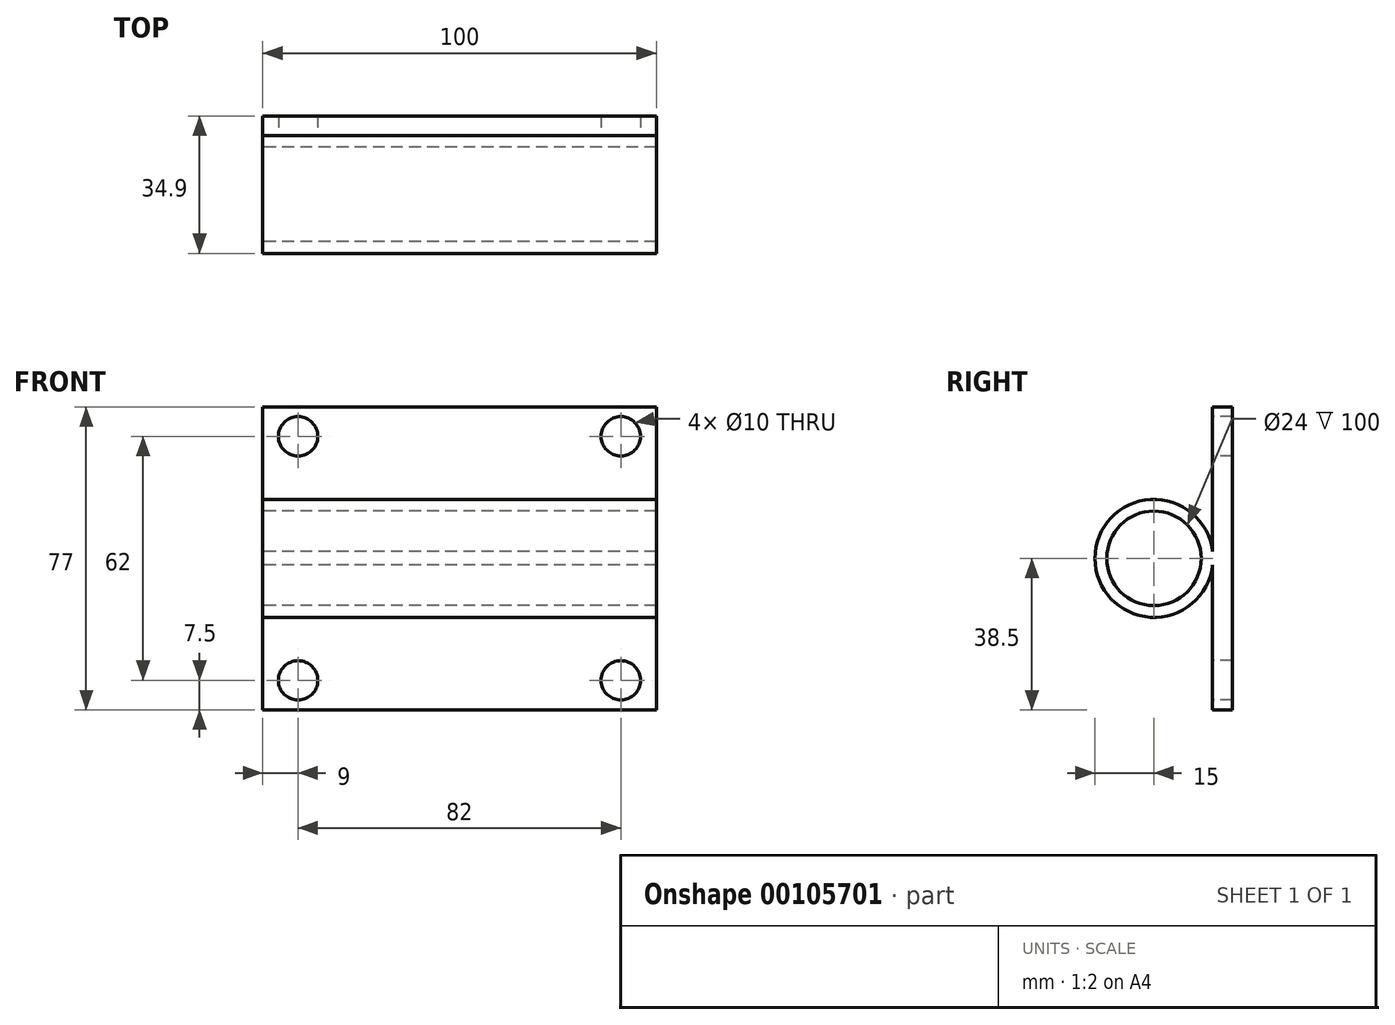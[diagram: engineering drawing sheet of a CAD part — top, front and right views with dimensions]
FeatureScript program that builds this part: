
annotation { "Feature Type Name" : "Feature", "Feature Type Description" : "" }
export const myFeature = defineFeature(function(context is Context, id is Id, definition is map)
    precondition{}
    {
        {
            var Q0;
            Q0=qCreatedBy(makeId("Front.planeOp"),FACE);
            var sketch = newSketch(context, id + "F0", { "sketchPlane" : qUnion([Q0])});
            skLineSegment(sketch, "E0.bottom", {"start": v(0, 0) * mm, "end": v(-100, 0) * mm});
            skLineSegment(sketch, "E0.top", {"start": v(0, 77) * mm, "end": v(-100, 77) * mm});
            skLineSegment(sketch, "E0.left", {"start": v(0, 0) * mm, "end": v(0, 77) * mm});
            skLineSegment(sketch, "E0.right", {"start": v(-100, 0) * mm, "end": v(-100, 77) * mm});
            skSolve(sketch);
        }
        {
            var Q0;
            Q0=makeQuery(id+"F0.imprint","IMPRINT",FACE,{"disambiguationData":[TD([[makeQuery(id+"F0.imprint","IMPRINT",EDGE,{"derivedFrom":sQuery(id+"F0.wireOp",EDGE,"E0.bottom")}),-1.0]])]});
            extrude(context, id + "F1", {"entities" : qUnion([Q0]), "depth" : 5 * mm});
        }
        {
            var Q0;
            Q0=makeQuery(id+"F1.opExtrude","CAP_FACE",FACE,{"disambiguationData":[OSD([sQuery(id+"F0.wireOp",EDGE,"E0.bottom"),sQuery(id+"F0.wireOp",EDGE,"E0.top"),sQuery(id+"F0.wireOp",EDGE,"E0.left"),sQuery(id+"F0.wireOp",EDGE,"E0.right")])],"isStart":false});
            var sketch = newSketch(context, id + "F2", { "sketchPlane" : qUnion([Q0])});
            skPoint(sketch, "E1", {"position": v(-91, 69.5) * mm});
            skPoint(sketch, "E2", {"position": v(-9, 69.5) * mm});
            skPoint(sketch, "E3", {"position": v(-9, 7.5) * mm});
            skPoint(sketch, "E4", {"position": v(-91, 7.5) * mm});
            skSolve(sketch);
        }
        {
            var Q0;
            Q0=sQuery(id+"F2.wireOp",VERTEX,"E1");
            var Q1;
            Q1=sQuery(id+"F2.wireOp",VERTEX,"E2");
            var Q2;
            Q2=sQuery(id+"F2.wireOp",VERTEX,"E4");
            var Q3;
            Q3=sQuery(id+"F2.wireOp",VERTEX,"E3");
            var Q4;
            Q4=makeQuery(id+"F1.opExtrude","SWEPT_BODY",BODY,{"disambiguationData":[OSD([sQuery(id+"F0.wireOp",EDGE,"E0.bottom"),sQuery(id+"F0.wireOp",EDGE,"E0.top"),sQuery(id+"F0.wireOp",EDGE,"E0.left"),sQuery(id+"F0.wireOp",EDGE,"E0.right")])]});
            hole(context, id + "F3", {"style" : HoleStyle.SIMPLE, "endStyle" : HoleEndStyle.THROUGH, "holeDiameter" : 10 * mm, "locations" : qUnion([Q0, Q1, Q2, Q3]), "scope" : qUnion([Q4]), "isTappedThrough" : true});
        }
        {
            var Q0;
            Q0=makeQuery(id+"F1.opExtrude","SWEPT_FACE",FACE,{"disambiguationData":[OSD([sQuery(id+"F0.wireOp",EDGE,"E0.right")])]});
            var sketch = newSketch(context, id + "F4", { "sketchPlane" : qUnion([Q0])});
            skCircle(sketch, "E5", {"center": v(19.9, 38.5) * mm, "radius": 12 * mm});
            skCircle(sketch, "E6", {"center": v(19.9, 38.5) * mm, "radius": 15 * mm});
            skSolve(sketch);
        }
        {
            var Q0;
            Q0=makeQuery(id+"F4.imprint","IMPRINT",FACE,{"disambiguationData":[TD([[makeQuery(id+"F4.imprint","IMPRINT",EDGE,{"derivedFrom":sQuery(id+"F4.wireOp",EDGE,"E5")}),-1.0]])]});
            var Q1;
            Q1=qCreatedBy(makeId("Right.planeOp"),FACE);
            extrude(context, id + "F5", {"entities" : qUnion([Q0]), "operationType" : NewBodyOperationType.ADD, "endBound" : BoundingType.UP_TO_SURFACE, "oppositeDirection" : true, "endBoundEntityFace" : qUnion([Q1]), "depth" : 25 * mm});
        }
    });
